# Revit family: AM 500 VC
name_source: partatom
category: Mechanical Equipment
units: mm (PartAtom-declared; Revit-internal decimal feet)

## family parameters
Always vertical = Yes
Cut with Voids When Loaded = No
OmniClass Number = 23.75.00.00
OmniClass Title = Climate Control (HVAC)
Part Type = Normal
Room Calculation Point = No
Round Connector Dimension = Use Diameter
Shared = No
Work Plane-Based = No

## types (1)
- AM 500 VC
    B-C Duct Exhaust = 328 mm  [stored 1.07612 ft]
    B-C Duct Supply = 328 mm  [stored 1.07612 ft]
    BMS IN = (PTS) 2x0,6
    BMS Out = (PTS) 2x2x0,6
    BMS Panel = (PTS) 2x2x0,6
    Condensate = 9 mm  [stored 0.0295276 ft]
    Electrical connection = 1 ~ 230 V / N / PE / 50 Hz
    Exhaust Air = 250 mm
    L-C Duct Exhaust = 238 mm  [stored 0.78084 ft]
    Manufacturer = Airmaster A/S
    Max. flow rate 30 dB(A) with ePM10 50% filters = 430 m³
    Max. flow rate 30 dB(A) with ePM10 55% filters = 387 m³
    Max. flow rate 30 dB(A) with ePM10 80% filters = 344 m³
    Max. flow rate 35 dB(A) with ePM10 50% filters = 550 m³
    Max. flow rate 35 dB(A) with ePM10 55% filters = 495 m³
    Max. flow rate 35 dB(A) with ePM10 80% filters = 440 m³
    Model = AM 500 VC
    Network Conection = AWG 24 CAT 5e STP
    Nominal current, air handling unit = 1,1 A
    Nominal current, electrical comfort heating surface = 2,6 A
    Nominal current, electrical preheating surface = 4,4 A
    Phase 1 - Max Current = 8,1 A
    Phase 1 - Max Power Consumption = 1762 W
    R-C Duct Supply = 192 mm  [stored 0.629921 ft]
    Suply Air In = 250 mm
    Total Depth = 779 mm  [stored 2.55577 ft]
    Total Hight = 439 mm  [stored 1.44029 ft]
    Total Width = 1600 mm  [stored 5.24934 ft]
    URL = www.airmaster-as.com
    Water Heater Surface IN = 10 mm  [stored 0.0328084 ft]
    Water Heater Surface Return = 10 mm  [stored 0.0328084 ft]
    Weight (Standard Unit) = 108

note: [stored X ft] marks values corroborated as IEEE doubles in the binary element streams (Revit-internal decimal feet)

## geometry (parser evidence)
native form markers: Sweep x6
no freeform markers — native parametric forms only
